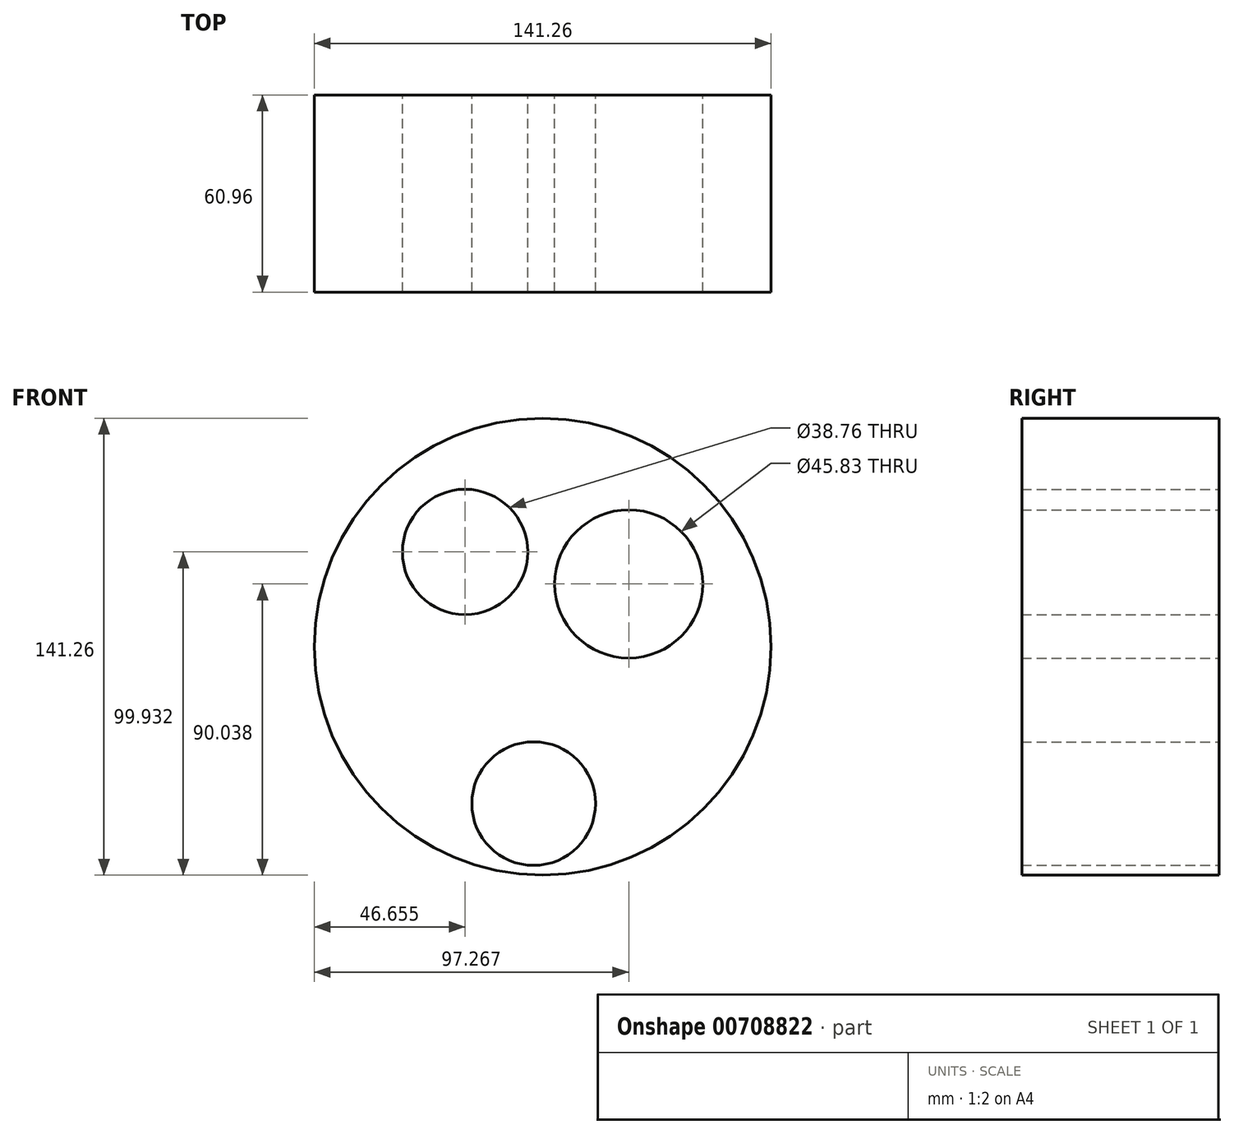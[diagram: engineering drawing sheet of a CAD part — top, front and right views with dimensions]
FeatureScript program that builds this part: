
annotation { "Feature Type Name" : "Feature", "Feature Type Description" : "" }
export const myFeature = defineFeature(function(context is Context, id is Id, definition is map)
    precondition{}
    {
        {
            var Q0;
            Q0=qCreatedBy(makeId("Front.planeOp"),FACE);
            var sketch = newSketch(context, id + "F0", { "sketchPlane" : qUnion([Q0])});
            skCircle(sketch, "E0", {"center": v(2.76, 0) * mm, "radius": 70.63 * mm});
            skCircle(sketch, "E1", {"center": v(-21.22, 29.3) * mm, "radius": 19.38 * mm});
            skCircle(sketch, "E2", {"center": v(29.4, 19.4) * mm, "radius": 22.91 * mm});
            skCircle(sketch, "E3", {"center": v(0, -48.52) * mm, "radius": 19.1 * mm});
            skSolve(sketch);
        }
        {
            var Q0;
            Q0=makeQuery(id+"F0.imprint","IMPRINT",FACE,{"disambiguationData":[TD([[makeQuery(id+"F0.imprint","IMPRINT",EDGE,{"derivedFrom":sQuery(id+"F0.wireOp",EDGE,"E0")}),1.0]])]});
            extrude(context, id + "F1", {"entities" : qUnion([Q0]), "depth" : 60.96 * mm, "offsetDistance" : 25.4 * mm});
        }
    });
